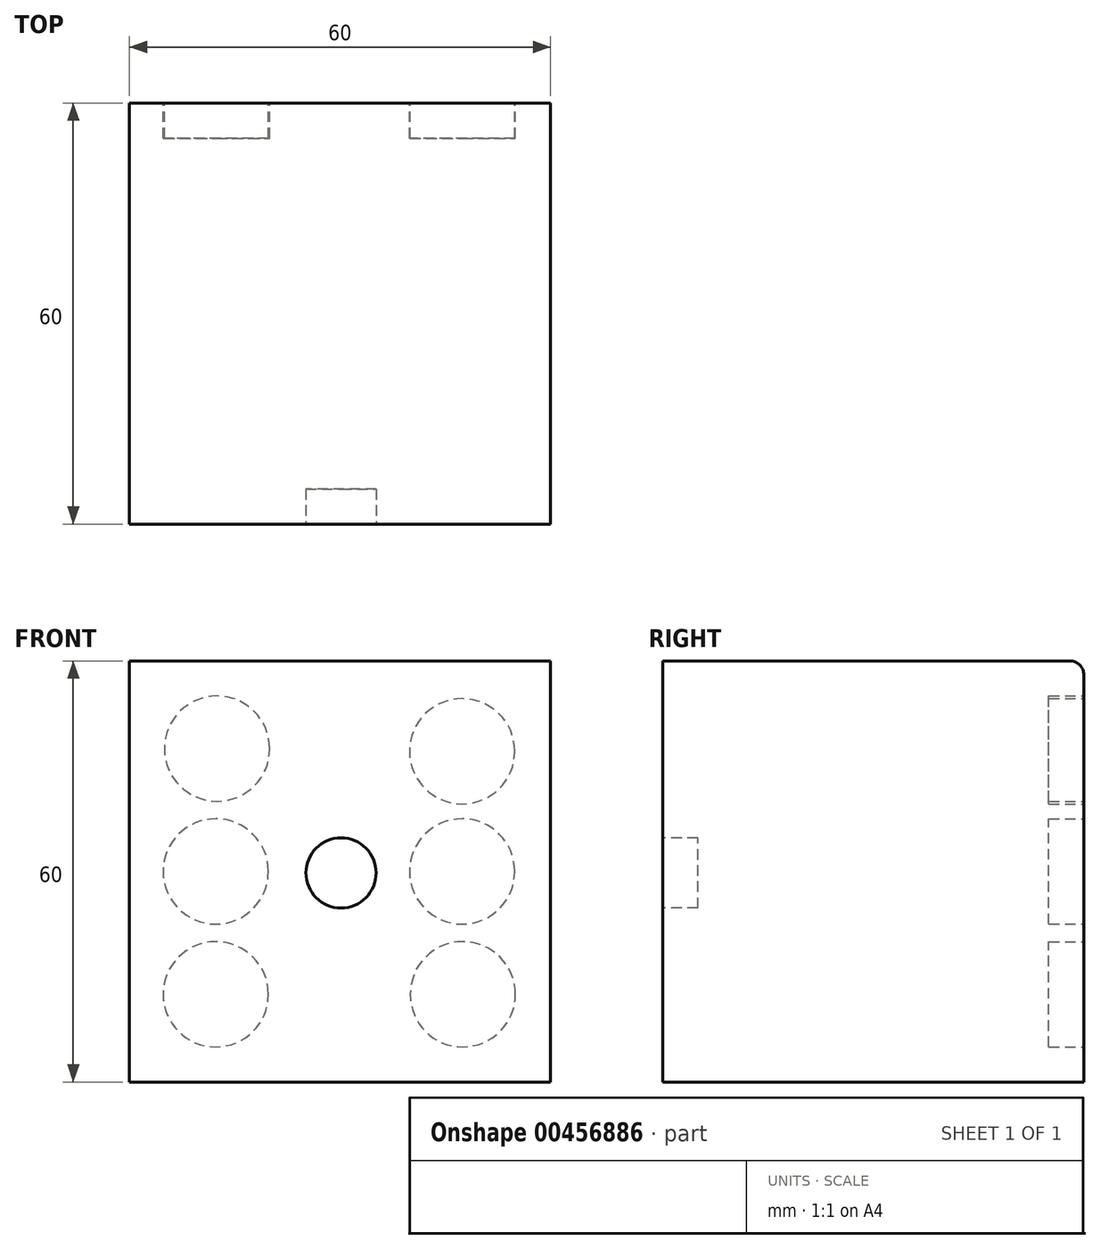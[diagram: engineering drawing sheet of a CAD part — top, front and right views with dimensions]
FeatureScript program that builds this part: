
annotation { "Feature Type Name" : "Feature", "Feature Type Description" : "" }
export const myFeature = defineFeature(function(context is Context, id is Id, definition is map)
    precondition{}
    {
        {
            var Q0;
            Q0=qCreatedBy(makeId("Front.planeOp"),FACE);
            var sketch = newSketch(context, id + "F0", { "sketchPlane" : qUnion([Q0])});
            skLineSegment(sketch, "E0.bottom", {"start": v(0, 0) * mm, "end": v(60, 0) * mm});
            skLineSegment(sketch, "E0.top", {"start": v(0, -60) * mm, "end": v(60, -60) * mm});
            skLineSegment(sketch, "E0.left", {"start": v(0, 0) * mm, "end": v(0, -60) * mm});
            skLineSegment(sketch, "E0.right", {"start": v(60, 0) * mm, "end": v(60, -60) * mm});
            skSolve(sketch);
        }
        {
            var Q0;
            Q0=qCreatedBy(makeId("Front.planeOp"),FACE);
            cPlane(context, id + "F1", {"entities" : qUnion([Q0]), "cplaneType" : CPlaneType.OFFSET, "offset" : 60 * mm, "width" : 150 * mm, "height" : 150 * mm});
        }
        {
            var Q0;
            Q0=qCreatedBy(id+"F1.planeOp",FACE);
            var sketch = newSketch(context, id + "F2", { "sketchPlane" : qUnion([Q0])});
            skLineSegment(sketch, "E1.bottom", {"start": v(0, 0) * mm, "end": v(60, 0) * mm});
            skLineSegment(sketch, "E1.top", {"start": v(0, -60) * mm, "end": v(60, -60) * mm});
            skLineSegment(sketch, "E1.left", {"start": v(0, 0) * mm, "end": v(0, -60) * mm});
            skLineSegment(sketch, "E1.right", {"start": v(60, 0) * mm, "end": v(60, -60) * mm});
            skSolve(sketch);
        }
        {
            var Q0;
            Q0 = qSketchRegion(id + "F0", true);
            var Q1;
            Q1 = qSketchRegion(id + "F2", true);
            loft(context, id + "F3", {"sheetProfilesArray" : [{ "sheetProfileEntities" : qUnion([Q0]) }, { "sheetProfileEntities" : qUnion([Q1]) }]});
        }
        {
            var Q0;
            Q0=qCreatedBy(id+"F1.planeOp",FACE);
            var sketch = newSketch(context, id + "F4", { "sketchPlane" : qUnion([Q0])});
            skLineSegment(sketch, "E2", {"start": v(0, -60.18) * mm, "end": v(60.3, 0) * mm});
            skLineSegment(sketch, "E3", {"start": v(60.3, -60.42) * mm, "end": v(0, 0) * mm});
            skSolve(sketch);
        }
        {
            var Q0;
            Q0=qCreatedBy(id+"F1.planeOp",FACE);
            var sketch = newSketch(context, id + "F5", { "sketchPlane" : qUnion([Q0])});
            skCircle(sketch, "E4", {"center": v(30.15, -30.2) * mm, "radius": 5 * mm});
            skSolve(sketch);
        }
        {
            var Q0;
            Q0 = qSketchRegion(id + "F5", true);
            extrude(context, id + "F6", {"entities" : qUnion([Q0]), "operationType" : NewBodyOperationType.REMOVE, "oppositeDirection" : true, "depth" : 5 * mm});
        }
        {
            var Q0;
            Q0=qCreatedBy(makeId("Front.planeOp"),FACE);
            var sketch = newSketch(context, id + "F7", { "sketchPlane" : qUnion([Q0])});
            skCircle(sketch, "E5", {"center": v(47.4, -12.87) * mm, "radius": 7.5 * mm});
            skCircle(sketch, "E6", {"center": v(12.48, -12.5) * mm, "radius": 7.5 * mm});
            skCircle(sketch, "E7", {"center": v(47.4, -30) * mm, "radius": 7.5 * mm});
            skCircle(sketch, "E8", {"center": v(12.3, -30) * mm, "radius": 7.5 * mm});
            skCircle(sketch, "E9", {"center": v(47.5, -47.5) * mm, "radius": 7.5 * mm});
            skLineSegment(sketch, "E10", {"start": v(65.27, -30) * mm, "end": v(-27.57, -30) * mm, "construction": true});
            skLineSegment(sketch, "E11", {"start": v(30, 10.1) * mm, "end": v(30, -65.26) * mm, "construction": true});
            skLineSegment(sketch, "E12", {"start": v(60, -60) * mm, "end": v(0, 0) * mm, "construction": true});
            skLineSegment(sketch, "E13", {"start": v(60, 0) * mm, "end": v(0, -60) * mm, "construction": true});
            skCircle(sketch, "E14", {"center": v(12.3, -47.5) * mm, "radius": 7.5 * mm});
            skLineSegment(sketch, "E15", {"start": v(47.5, 4.36) * mm, "end": v(47.5, -58.35) * mm, "construction": true});
            skLineSegment(sketch, "E16", {"start": v(12.3, 4.08) * mm, "end": v(12.3, -55.61) * mm, "construction": true});
            skLineSegment(sketch, "E17", {"start": v(65.95, -12.5) * mm, "end": v(-11.13, -12.5) * mm, "construction": true});
            skLineSegment(sketch, "E18", {"start": v(64.63, -47.5) * mm, "end": v(-18.3, -47.5) * mm, "construction": true});
            skSolve(sketch);
        }
        {
            var Q0;
            Q0 = qSketchRegion(id + "F7", true);
            extrude(context, id + "F8", {"entities" : qUnion([Q0]), "operationType" : NewBodyOperationType.REMOVE, "depth" : 5 * mm});
        }
        {
            var Q0;
            Q0=makeQuery(id+"F3.opLoft","MID_CAP_EDGE",EDGE,{"disambiguationData":[OSD([sQuery(id+"F0.wireOp",EDGE,"E0.bottom"),sQuery(id+"F0.wireOp",EDGE,"E0.left"),sQuery(id+"F0.wireOp",EDGE,"E0.right")])],"capPos":0.0});
            fillet(context, id + "F9", {"entities" : qUnion([Q0]), "radius" : 2 * mm, "tangentPropagation" : true, "allowEdgeOverflow" : false});
        }
    });
